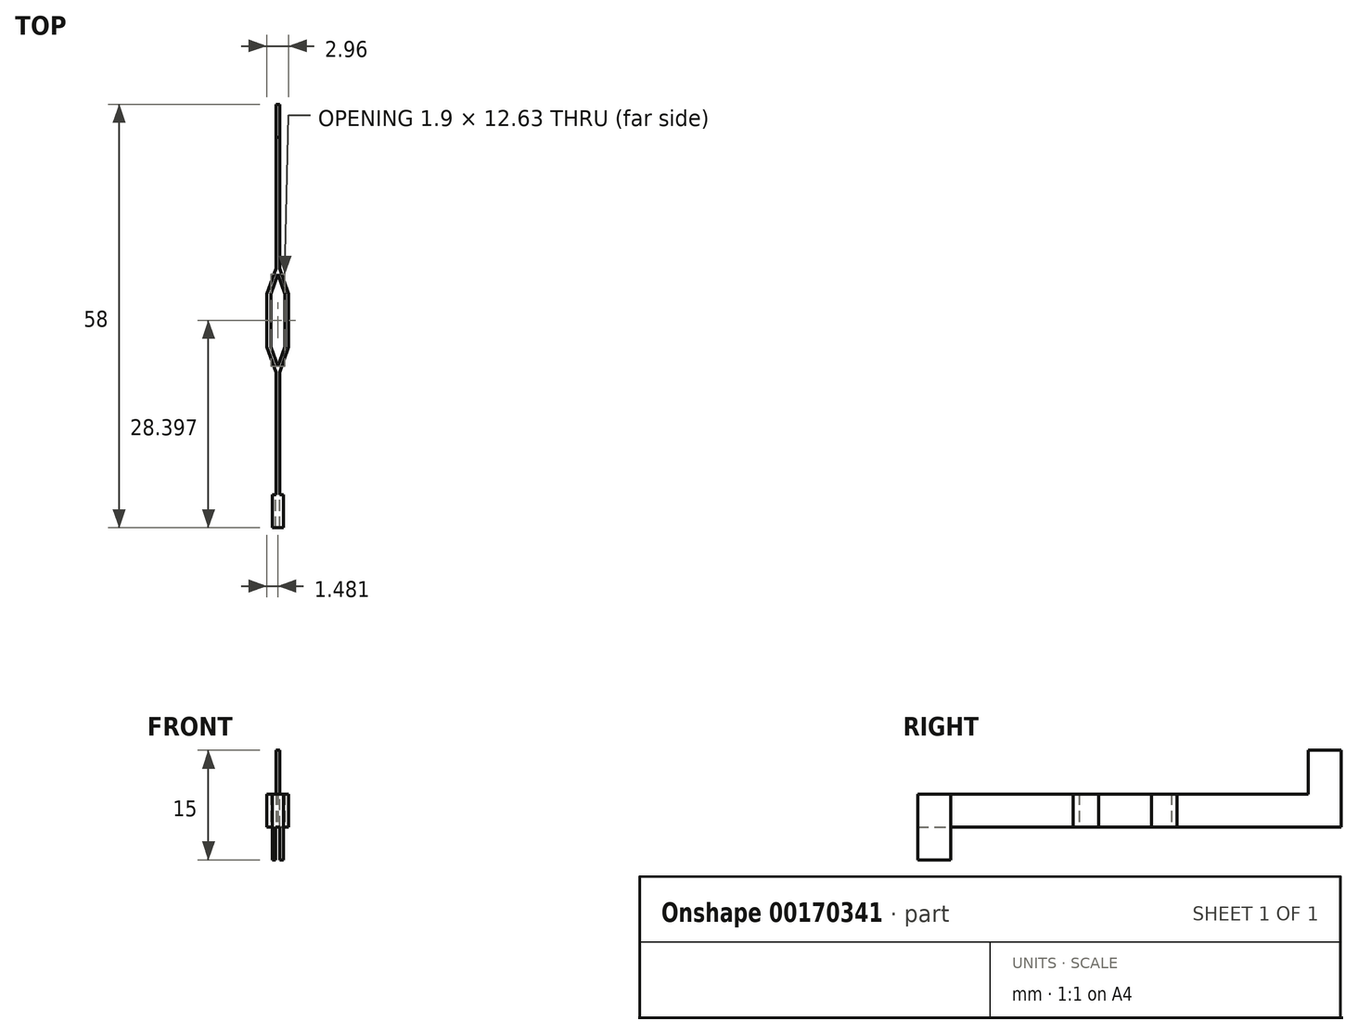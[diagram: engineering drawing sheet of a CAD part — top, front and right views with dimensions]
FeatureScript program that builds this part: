
annotation { "Feature Type Name" : "Feature", "Feature Type Description" : "" }
export const myFeature = defineFeature(function(context is Context, id is Id, definition is map)
    precondition{}
    {
        {
            var Q0;
            Q0=qCreatedBy(makeId("Top.planeOp"),FACE);
            var sketch = newSketch(context, id + "F0", { "sketchPlane" : qUnion([Q0])});
            skLineSegment(sketch, "E0.bottom", {"start": v(-0.97, 31.3) * mm, "end": v(-0.47, 31.3) * mm});
            skLineSegment(sketch, "E0.top", {"start": v(-0.97, -26.7) * mm, "end": v(-0.47, -26.7) * mm});
            skLineSegment(sketch, "E1.bottom", {"start": v(-1.67, 5.3) * mm, "end": v(0.23, 5.3) * mm});
            skLineSegment(sketch, "E1.top", {"start": v(-1.67, -1.9) * mm, "end": v(0.23, -1.9) * mm});
            skLineSegment(sketch, "E1.left", {"start": v(-1.67, 5.3) * mm, "end": v(-1.67, -1.9) * mm});
            skLineSegment(sketch, "E1.right", {"start": v(0.23, 5.3) * mm, "end": v(0.23, -1.9) * mm});
            skLineSegment(sketch, "E2", {"start": v(-1.67, 5.3) * mm, "end": v(-0.97, 7.3) * mm});
            skLineSegment(sketch, "E3", {"start": v(-0.47, 7.3) * mm, "end": v(0.23, 5.3) * mm});
            skLineSegment(sketch, "E4", {"start": v(-1.67, -1.9) * mm, "end": v(-0.97, -3.9) * mm});
            skLineSegment(sketch, "E5", {"start": v(-0.47, -3.9) * mm, "end": v(0.23, -1.9) * mm});
            skLineSegment(sketch, "E6", {"start": v(-0.97, 8.82) * mm, "end": v(-2.2, 5.3) * mm});
            skLineSegment(sketch, "E7", {"start": v(-2.2, 5.3) * mm, "end": v(-2.2, -1.9) * mm});
            skLineSegment(sketch, "E8", {"start": v(-2.2, -1.9) * mm, "end": v(-0.97, -5.4) * mm});
            skLineSegment(sketch, "E9", {"start": v(-0.47, 8.82) * mm, "end": v(0.76, 5.3) * mm});
            skLineSegment(sketch, "E10", {"start": v(0.76, 5.3) * mm, "end": v(0.76, -1.9) * mm});
            skLineSegment(sketch, "E11", {"start": v(0.76, -1.9) * mm, "end": v(-0.47, -5.4) * mm});
            skLineSegment(sketch, "E12", {"start": v(-0.97, 31.3) * mm, "end": v(-0.97, 8.82) * mm});
            skLineSegment(sketch, "E13", {"start": v(-0.97, -5.4) * mm, "end": v(-0.97, -26.7) * mm});
            skLineSegment(sketch, "E14", {"start": v(-0.47, 31.3) * mm, "end": v(-0.47, 8.82) * mm});
            skLineSegment(sketch, "E15", {"start": v(-0.47, -5.4) * mm, "end": v(-0.47, -26.7) * mm});
            skLineSegment(sketch, "E16", {"start": v(-0.47, 7.3) * mm, "end": v(-0.72, 8.02) * mm});
            skLineSegment(sketch, "E17", {"start": v(-0.72, 8.02) * mm, "end": v(-0.97, 7.3) * mm});
            skLineSegment(sketch, "E18", {"start": v(-0.47, -3.9) * mm, "end": v(-0.72, -4.6) * mm});
            skLineSegment(sketch, "E19", {"start": v(-0.97, -3.9) * mm, "end": v(-0.72, -4.6) * mm});
            skSolve(sketch);
        }
        {
            var Q0;
            Q0=makeQuery(id+"F0.imprint","IMPRINT",FACE,{"disambiguationData":[TD([[makeQuery(id+"F0.imprint","IMPRINT",EDGE,{"derivedFrom":sQuery(id+"F0.wireOp",EDGE,"E0.bottom")}),-1.0]])]});
            var Q1;
            Q1=sQuery(id+"F0.wireOp",EDGE,"E3");
            var Q2;
            Q2=sQuery(id+"F0.wireOp",EDGE,"E1.right");
            var Q3;
            Q3=sQuery(id+"F0.wireOp",EDGE,"E5");
            var Q4;
            Q4=sQuery(id+"F0.wireOp",EDGE,"nkD4Ib0B-5Y8a-obz0-IcfC-dqy6glZyB51n");
            var Q5;
            Q5=sQuery(id+"F0.wireOp",EDGE,"diSldYqd-0EJK-Tftk-uqzO-esxdoyUf5riP");
            var Q6;
            Q6=sQuery(id+"F0.wireOp",EDGE,"E1.left");
            var Q7;
            Q7=sQuery(id+"F0.wireOp",EDGE,"E2");
            var Q8;
            Q8=sQuery(id+"F0.wireOp",EDGE,"E4");
            var Q9;
            Q9=sQuery(id+"F0.wireOp",EDGE,"E8");
            var Q10;
            Q10=sQuery(id+"F0.wireOp",EDGE,"E7");
            var Q11;
            Q11=sQuery(id+"F0.wireOp",EDGE,"E10");
            var Q12;
            Q12=sQuery(id+"F0.wireOp",EDGE,"E11");
            var Q13;
            Q13=sQuery(id+"F0.wireOp",EDGE,"E14");
            var Q14;
            Q14=sQuery(id+"F0.wireOp",EDGE,"E12");
            var Q15;
            Q15=sQuery(id+"F0.wireOp",EDGE,"E6");
            var Q16;
            Q16=sQuery(id+"F0.wireOp",EDGE,"E9");
            var Q17;
            Q17=sQuery(id+"F0.wireOp",EDGE,"E0.bottom");
            var Q18;
            Q18=sQuery(id+"F0.wireOp",EDGE,"E15");
            var Q19;
            Q19=sQuery(id+"F0.wireOp",EDGE,"E13");
            var Q20;
            Q20=sQuery(id+"F0.wireOp",EDGE,"E0.top");
            extrude(context, id + "F1", {"entities" : qUnion([Q0]), "surfaceEntities" : qUnion([Q1, Q2, Q3, Q4, Q5, Q6, Q7, Q8, Q9, Q10, Q11, Q12, Q13, Q14, Q15, Q16, Q17, Q18, Q19, Q20]), "depth" : 4.5 * mm});
        }
        {
            var Q0;
            Q0=makeQuery(id+"F1.opExtrude","CAP_FACE",FACE,{"disambiguationData":[OSD([sQuery(id+"F0.wireOp",EDGE,"E0.bottom"),sQuery(id+"F0.wireOp",EDGE,"E0.top"),sQuery(id+"F0.wireOp",EDGE,"E1.left"),sQuery(id+"F0.wireOp",EDGE,"E1.right"),sQuery(id+"F0.wireOp",EDGE,"E2"),sQuery(id+"F0.wireOp",EDGE,"E3"),sQuery(id+"F0.wireOp",EDGE,"E4"),sQuery(id+"F0.wireOp",EDGE,"E5"),sQuery(id+"F0.wireOp",EDGE,"E6"),sQuery(id+"F0.wireOp",EDGE,"E7"),sQuery(id+"F0.wireOp",EDGE,"E8"),sQuery(id+"F0.wireOp",EDGE,"E9"),sQuery(id+"F0.wireOp",EDGE,"E10"),sQuery(id+"F0.wireOp",EDGE,"E11"),sQuery(id+"F0.wireOp",EDGE,"E12"),sQuery(id+"F0.wireOp",EDGE,"E13"),sQuery(id+"F0.wireOp",EDGE,"E14"),sQuery(id+"F0.wireOp",EDGE,"E15"),sQuery(id+"F0.wireOp",EDGE,"E16"),sQuery(id+"F0.wireOp",EDGE,"E17"),sQuery(id+"F0.wireOp",EDGE,"E18"),sQuery(id+"F0.wireOp",EDGE,"E19")])],"isStart":false});
            var sketch = newSketch(context, id + "F2", { "sketchPlane" : qUnion([Q0])});
            skLineSegment(sketch, "E20.bottom", {"start": v(-0.97, 31.3) * mm, "end": v(-0.47, 31.3) * mm});
            skLineSegment(sketch, "E20.top", {"start": v(-0.97, 26.8) * mm, "end": v(-0.47, 26.8) * mm});
            skLineSegment(sketch, "E20.left", {"start": v(-0.97, 31.3) * mm, "end": v(-0.97, 26.8) * mm});
            skLineSegment(sketch, "E20.right", {"start": v(-0.47, 31.3) * mm, "end": v(-0.47, 26.8) * mm});
            skSolve(sketch);
        }
        {
            var Q0;
            Q0=makeQuery(id+"F2.imprint","IMPRINT",FACE,{"disambiguationData":[TD([[makeQuery(id+"F2.imprint","IMPRINT",EDGE,{"derivedFrom":sQuery(id+"F2.wireOp",EDGE,"E20.bottom")}),-1.0]])]});
            extrude(context, id + "F3", {"entities" : qUnion([Q0]), "operationType" : NewBodyOperationType.ADD, "depth" : 6 * mm});
        }
        {
            var Q0;
            Q0=makeQuery(id+"F1.opExtrude","CAP_FACE",FACE,{"disambiguationData":[OSD([sQuery(id+"F0.wireOp",EDGE,"E0.bottom"),sQuery(id+"F0.wireOp",EDGE,"E0.top"),sQuery(id+"F0.wireOp",EDGE,"E1.left"),sQuery(id+"F0.wireOp",EDGE,"E1.right"),sQuery(id+"F0.wireOp",EDGE,"E2"),sQuery(id+"F0.wireOp",EDGE,"E3"),sQuery(id+"F0.wireOp",EDGE,"E4"),sQuery(id+"F0.wireOp",EDGE,"E5"),sQuery(id+"F0.wireOp",EDGE,"E6"),sQuery(id+"F0.wireOp",EDGE,"E7"),sQuery(id+"F0.wireOp",EDGE,"E8"),sQuery(id+"F0.wireOp",EDGE,"E9"),sQuery(id+"F0.wireOp",EDGE,"E10"),sQuery(id+"F0.wireOp",EDGE,"E11"),sQuery(id+"F0.wireOp",EDGE,"E12"),sQuery(id+"F0.wireOp",EDGE,"E13"),sQuery(id+"F0.wireOp",EDGE,"E14"),sQuery(id+"F0.wireOp",EDGE,"E15"),sQuery(id+"F0.wireOp",EDGE,"E16"),sQuery(id+"F0.wireOp",EDGE,"E17"),sQuery(id+"F0.wireOp",EDGE,"E18"),sQuery(id+"F0.wireOp",EDGE,"E19")])],"isStart":false});
            var sketch = newSketch(context, id + "F4", { "sketchPlane" : qUnion([Q0])});
            skLineSegment(sketch, "E21.bottom", {"start": v(-0.47, -26.7) * mm, "end": v(0.03, -26.7) * mm});
            skLineSegment(sketch, "E21.top", {"start": v(-0.47, -22.2) * mm, "end": v(0.03, -22.2) * mm});
            skLineSegment(sketch, "E21.left", {"start": v(-0.47, -26.7) * mm, "end": v(-0.47, -22.2) * mm});
            skLineSegment(sketch, "E21.right", {"start": v(0.03, -26.7) * mm, "end": v(0.03, -22.2) * mm});
            skLineSegment(sketch, "E22.bottom", {"start": v(-0.97, -26.7) * mm, "end": v(-1.47, -26.7) * mm});
            skLineSegment(sketch, "E22.top", {"start": v(-0.97, -22.2) * mm, "end": v(-1.47, -22.2) * mm});
            skLineSegment(sketch, "E22.left", {"start": v(-0.97, -26.7) * mm, "end": v(-0.97, -22.2) * mm});
            skLineSegment(sketch, "E22.right", {"start": v(-1.47, -26.7) * mm, "end": v(-1.47, -22.2) * mm});
            skSolve(sketch);
        }
        {
            var Q0;
            Q0=makeQuery(id+"F4.imprint","IMPRINT",FACE,{"disambiguationData":[TD([[makeQuery(id+"F4.imprint","IMPRINT",EDGE,{"derivedFrom":sQuery(id+"F4.wireOp",EDGE,"E21.bottom")}),1.0]])]});
            var Q1;
            Q1=makeQuery(id+"F4.imprint","IMPRINT",FACE,{"disambiguationData":[TD([[makeQuery(id+"F4.imprint","IMPRINT",EDGE,{"derivedFrom":sQuery(id+"F4.wireOp",EDGE,"E22.bottom")}),-1.0]])]});
            extrude(context, id + "F5", {"entities" : qUnion([Q0, Q1]), "operationType" : NewBodyOperationType.ADD, "oppositeDirection" : true, "depth" : 9 * mm});
        }
        {
            var Q0;
            Q0=makeQuery(id+"F1.opExtrude","CAP_FACE",FACE,{"disambiguationData":[OSD([sQuery(id+"F0.wireOp",EDGE,"E0.bottom"),sQuery(id+"F0.wireOp",EDGE,"E0.top"),sQuery(id+"F0.wireOp",EDGE,"E1.left"),sQuery(id+"F0.wireOp",EDGE,"E1.right"),sQuery(id+"F0.wireOp",EDGE,"E2"),sQuery(id+"F0.wireOp",EDGE,"E3"),sQuery(id+"F0.wireOp",EDGE,"E4"),sQuery(id+"F0.wireOp",EDGE,"E5"),sQuery(id+"F0.wireOp",EDGE,"E6"),sQuery(id+"F0.wireOp",EDGE,"E7"),sQuery(id+"F0.wireOp",EDGE,"E8"),sQuery(id+"F0.wireOp",EDGE,"E9"),sQuery(id+"F0.wireOp",EDGE,"E10"),sQuery(id+"F0.wireOp",EDGE,"E11"),sQuery(id+"F0.wireOp",EDGE,"E12"),sQuery(id+"F0.wireOp",EDGE,"E13"),sQuery(id+"F0.wireOp",EDGE,"E14"),sQuery(id+"F0.wireOp",EDGE,"E15"),sQuery(id+"F0.wireOp",EDGE,"E16"),sQuery(id+"F0.wireOp",EDGE,"E17"),sQuery(id+"F0.wireOp",EDGE,"E18"),sQuery(id+"F0.wireOp",EDGE,"E19")])],"isStart":true});
            var sketch = newSketch(context, id + "F6", { "sketchPlane" : qUnion([Q0])});
            skLineSegment(sketch, "E23.bottom", {"start": v(-1.02, 26.7) * mm, "end": v(-0.42, 26.7) * mm});
            skLineSegment(sketch, "E23.top", {"start": v(-1.02, 22.2) * mm, "end": v(-0.42, 22.2) * mm});
            skLineSegment(sketch, "E23.left", {"start": v(-1.02, 26.7) * mm, "end": v(-1.02, 22.2) * mm});
            skLineSegment(sketch, "E23.right", {"start": v(-0.42, 26.7) * mm, "end": v(-0.42, 22.2) * mm});
            skSolve(sketch);
        }
        {
            var Q0;
            Q0 = qSketchRegion(id + "F6", true);
            extrude(context, id + "F7", {"entities" : qUnion([Q0]), "operationType" : NewBodyOperationType.REMOVE, "depth" : 25 * mm});
        }
    });
